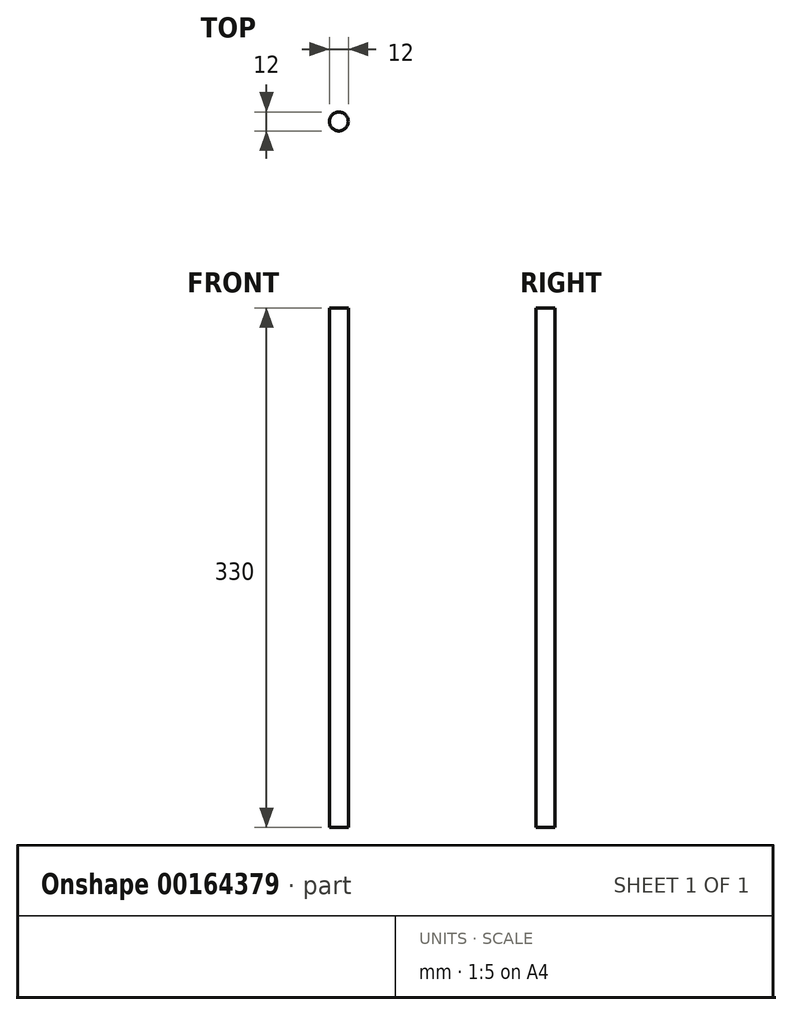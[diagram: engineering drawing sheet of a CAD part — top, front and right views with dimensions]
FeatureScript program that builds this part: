
annotation { "Feature Type Name" : "Feature", "Feature Type Description" : "" }
export const myFeature = defineFeature(function(context is Context, id is Id, definition is map)
    precondition{}
    {
        {
            var Q0;
            Q0=qCreatedBy(makeId("Top.planeOp"),FACE);
            var sketch = newSketch(context, id + "F0", { "sketchPlane" : qUnion([Q0])});
            skCircle(sketch, "E0", {"center": v(0, 0) * mm, "radius": 6 * mm});
            skSolve(sketch);
        }
        {
            var Q0;
            Q0 = qSketchRegion(id + "F0", true);
            extrude(context, id + "F1", {"entities" : qUnion([Q0]), "depth" : 330 * mm});
        }
    });
